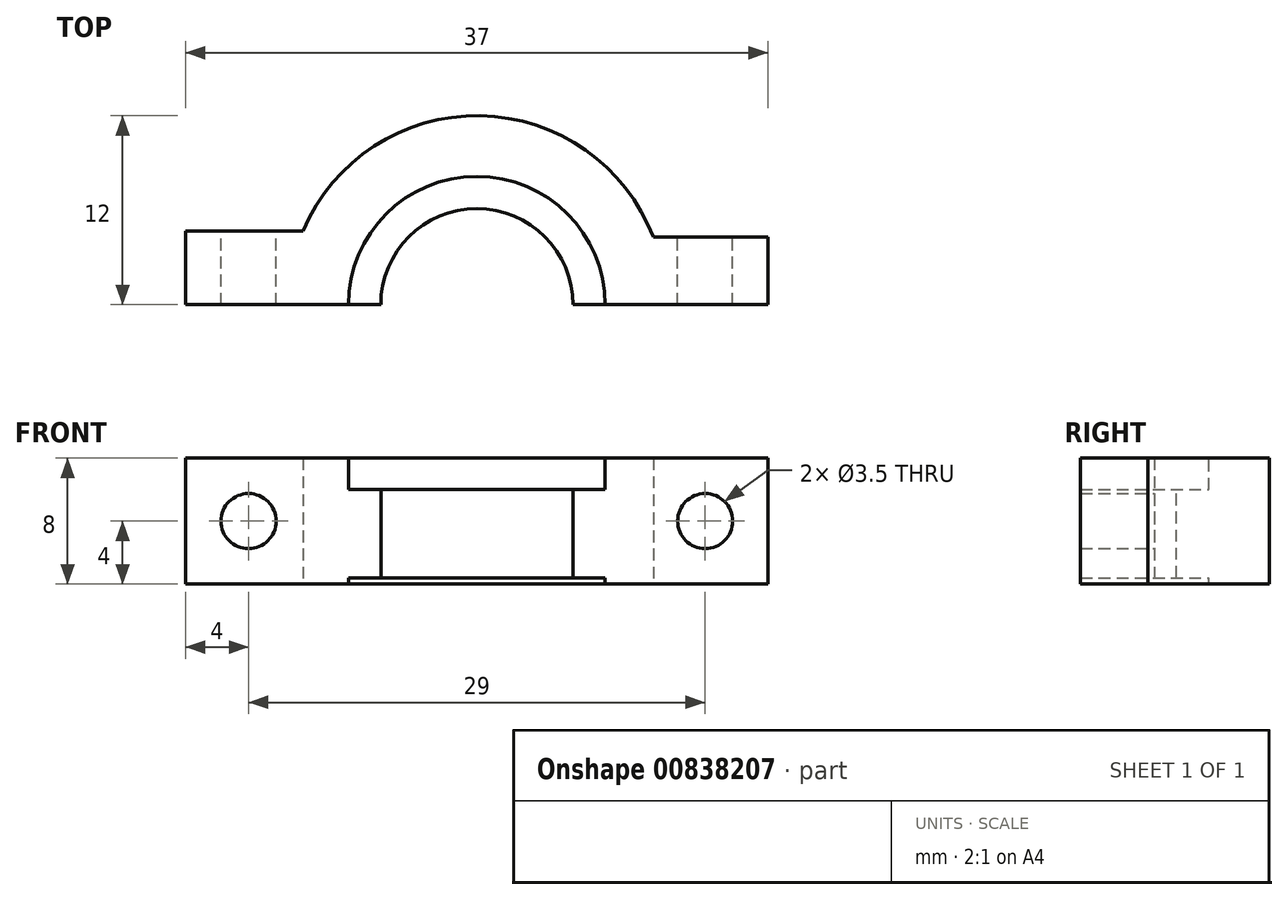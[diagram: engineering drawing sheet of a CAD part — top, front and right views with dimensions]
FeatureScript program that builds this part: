
annotation { "Feature Type Name" : "Feature", "Feature Type Description" : "" }
export const myFeature = defineFeature(function(context is Context, id is Id, definition is map)
    precondition{}
    {
        {
            var Q0;
            Q0=qCreatedBy(makeId("Top.planeOp"),FACE);
            var sketch = newSketch(context, id + "F0", { "sketchPlane" : qUnion([Q0])});
            skCircle(sketch, "E0", {"center": v(0, 0) * mm, "radius": 8.15 * mm, "construction": true});
            skArc(sketch, "E1", {"start": v(11.2, 4.28) * mm, "mid": v(0.22, 12) * mm, "end": v(-11.05, 4.68) * mm});
            skLineSegment(sketch, "E2", {"start": v(-12, 0) * mm, "end": v(-18.5, 0) * mm});
            skLineSegment(sketch, "E3", {"start": v(12, 0) * mm, "end": v(18.5, 0) * mm});
            skLineSegment(sketch, "E4", {"start": v(18.5, 0) * mm, "end": v(18.5, 4.28) * mm});
            skLineSegment(sketch, "E5", {"start": v(18.5, 4.28) * mm, "end": v(11.2, 4.28) * mm});
            skLineSegment(sketch, "E6", {"start": v(-18.5, 0) * mm, "end": v(-18.5, 4.68) * mm});
            skLineSegment(sketch, "E7", {"start": v(-18.5, 4.68) * mm, "end": v(-11.05, 4.68) * mm});
            skLineSegment(sketch, "E8", {"start": v(-12, 0) * mm, "end": v(12, 0) * mm});
            skSolve(sketch);
        }
        {
            var Q0;
            Q0 = qSketchRegion(id + "F0", true);
            extrude(context, id + "F1", {"entities" : qUnion([Q0]), "depth" : 8 * mm, "offsetDistance" : 25 * mm});
        }
        {
            var Q0;
            Q0=makeQuery(id+"F1.opExtrude","SWEPT_FACE",FACE,{"disambiguationData":[OSD([sQuery(id+"F0.wireOp",EDGE,"E5")])]});
            var sketch = newSketch(context, id + "F2", { "sketchPlane" : qUnion([Q0])});
            skCircle(sketch, "E9", {"center": v(-14.5, 4) * mm, "radius": 1.75 * mm});
            skCircle(sketch, "E10", {"center": v(14.5, 4) * mm, "radius": 1.75 * mm});
            skSolve(sketch);
        }
        {
            var Q0;
            Q0 = qSketchRegion(id + "F2", true);
            extrude(context, id + "F3", {"entities" : qUnion([Q0]), "operationType" : NewBodyOperationType.REMOVE, "endBound" : BoundingType.THROUGH_ALL, "oppositeDirection" : true, "depth" : 25 * mm, "offsetDistance" : 25 * mm});
        }
        {
            var Q0;
            Q0=makeQuery(id+"F1.opExtrude","SWEPT_FACE",FACE,{"disambiguationData":[OSD([sQuery(id+"F0.wireOp",EDGE,"E7")])]});
            var sketch = newSketch(context, id + "F4", { "sketchPlane" : qUnion([Q0])});
            skCircle(sketch, "E11", {"center": v(14.5, 4) * mm, "radius": 1.75 * mm});
            skSolve(sketch);
        }
        {
            var Q0;
            Q0 = qSketchRegion(id + "F4", true);
            extrude(context, id + "F5", {"entities" : qUnion([Q0]), "operationType" : NewBodyOperationType.REMOVE, "oppositeDirection" : true, "depth" : 25 * mm, "offsetDistance" : 25 * mm});
        }
        {
            var Q0;
            Q0=makeQuery(id+"F1.opExtrude","CAP_FACE",FACE,{"disambiguationData":[OSD([sQuery(id+"F0.wireOp",EDGE,"E1"),sQuery(id+"F0.wireOp",EDGE,"E2"),sQuery(id+"F0.wireOp",EDGE,"E3"),sQuery(id+"F0.wireOp",EDGE,"E4"),sQuery(id+"F0.wireOp",EDGE,"E5"),sQuery(id+"F0.wireOp",EDGE,"E6"),sQuery(id+"F0.wireOp",EDGE,"E7"),sQuery(id+"F0.wireOp",EDGE,"E8")])],"isStart":false});
            var sketch = newSketch(context, id + "F6", { "sketchPlane" : qUnion([Q0])});
            skCircle(sketch, "E12", {"center": v(0, 0) * mm, "radius": 8.15 * mm});
            skSolve(sketch);
        }
        {
            var Q0;
            Q0 = qSketchRegion(id + "F6", true);
            extrude(context, id + "F7", {"entities" : qUnion([Q0]), "operationType" : NewBodyOperationType.REMOVE, "oppositeDirection" : true, "depth" : 2 * mm, "offsetDistance" : 25 * mm});
        }
        {
            var Q0;
            Q0=makeQuery(id+"F7.boolean.opBoolean","COPY",FACE,{"derivedFrom":makeQuery(id+"F7.opExtrude","CAP_FACE",FACE,{"disambiguationData":[OSD([sQuery(id+"F6.wireOp",EDGE,"E12")])],"isStart":false})});
            var sketch = newSketch(context, id + "F8", { "sketchPlane" : qUnion([Q0])});
            skCircle(sketch, "E13", {"center": v(0, 0) * mm, "radius": 6.1 * mm});
            skSolve(sketch);
        }
        {
            var Q0;
            Q0 = qSketchRegion(id + "F8", true);
            extrude(context, id + "F9", {"entities" : qUnion([Q0]), "operationType" : NewBodyOperationType.REMOVE, "oppositeDirection" : true, "depth" : 5.6 * mm, "offsetDistance" : 25 * mm});
        }
        {
            var Q0;
            Q0=makeQuery(id+"F9.boolean.opBoolean","COPY",FACE,{"derivedFrom":makeQuery(id+"F9.opExtrude","CAP_FACE",FACE,{"disambiguationData":[OSD([sQuery(id+"F8.wireOp",EDGE,"E13")])],"isStart":false})});
            var sketch = newSketch(context, id + "F10", { "sketchPlane" : qUnion([Q0])});
            skCircle(sketch, "E14", {"center": v(0, 0) * mm, "radius": 8.15 * mm});
            skSolve(sketch);
        }
        {
            var Q0;
            Q0 = qSketchRegion(id + "F10", true);
            extrude(context, id + "F11", {"entities" : qUnion([Q0]), "operationType" : NewBodyOperationType.REMOVE, "oppositeDirection" : true, "depth" : 25 * mm, "offsetDistance" : 25 * mm});
        }
    });
